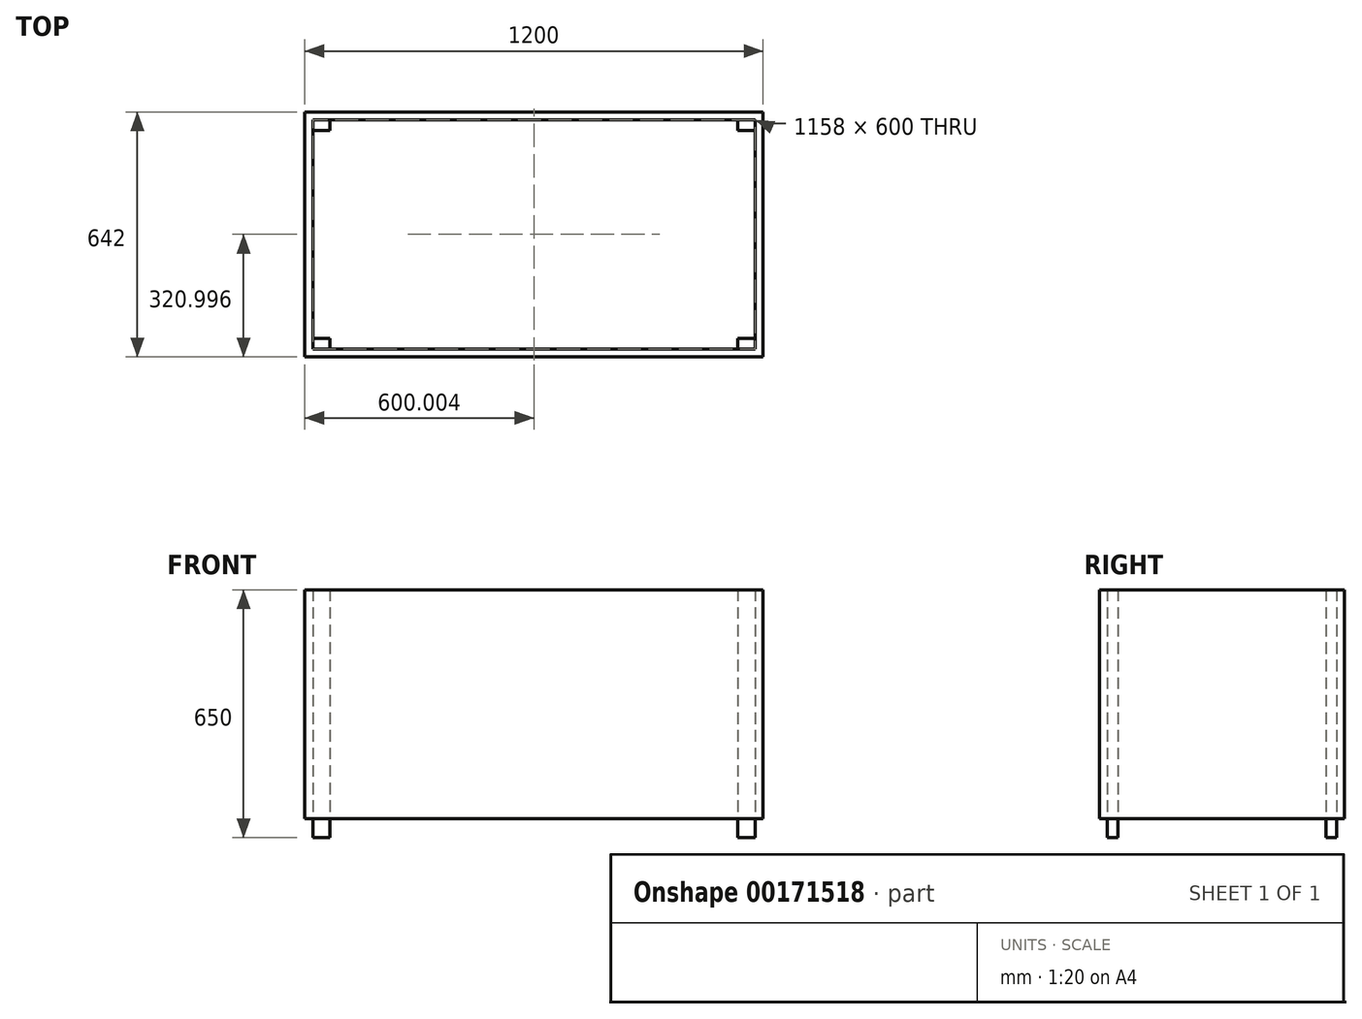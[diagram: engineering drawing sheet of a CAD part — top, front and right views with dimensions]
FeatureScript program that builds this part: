
annotation { "Feature Type Name" : "Feature", "Feature Type Description" : "" }
export const myFeature = defineFeature(function(context is Context, id is Id, definition is map)
    precondition{}
    {
        {
            var Q0;
            Q0=qCreatedBy(makeId("Top.planeOp"),FACE);
            var sketch = newSketch(context, id + "F0", { "sketchPlane" : qUnion([Q0])});
            skLineSegment(sketch, "E0.bottom", {"start": v(-516.42, -156.54) * mm, "end": v(683.58, -156.54) * mm});
            skLineSegment(sketch, "E0.top", {"start": v(-516.42, -177.54) * mm, "end": v(683.58, -177.54) * mm});
            skLineSegment(sketch, "E0.left", {"start": v(-516.42, -156.54) * mm, "end": v(-516.42, -177.54) * mm});
            skLineSegment(sketch, "E0.right", {"start": v(683.58, -156.54) * mm, "end": v(683.58, -177.54) * mm});
            skLineSegment(sketch, "E1.bottom", {"start": v(683.58, 464.46) * mm, "end": v(-516.42, 464.46) * mm});
            skLineSegment(sketch, "E1.top", {"start": v(683.58, 443.46) * mm, "end": v(-516.42, 443.46) * mm});
            skLineSegment(sketch, "E1.left", {"start": v(683.58, 464.46) * mm, "end": v(683.58, 443.46) * mm});
            skLineSegment(sketch, "E1.right", {"start": v(-516.42, 464.46) * mm, "end": v(-516.42, 443.46) * mm});
            skLineSegment(sketch, "E2.bottom", {"start": v(-516.42, 443.46) * mm, "end": v(-495.42, 443.46) * mm});
            skLineSegment(sketch, "E2.top", {"start": v(-516.42, -156.54) * mm, "end": v(-495.42, -156.54) * mm});
            skLineSegment(sketch, "E2.left", {"start": v(-516.42, 443.46) * mm, "end": v(-516.42, -156.54) * mm});
            skLineSegment(sketch, "E2.right", {"start": v(-495.42, 443.46) * mm, "end": v(-495.42, -156.54) * mm});
            skLineSegment(sketch, "E3.bottom", {"start": v(662.58, 443.46) * mm, "end": v(683.58, 443.46) * mm});
            skLineSegment(sketch, "E3.top", {"start": v(662.58, -156.54) * mm, "end": v(683.58, -156.54) * mm});
            skLineSegment(sketch, "E3.left", {"start": v(662.58, 443.46) * mm, "end": v(662.58, -156.54) * mm});
            skLineSegment(sketch, "E3.right", {"start": v(683.58, 443.46) * mm, "end": v(683.58, -156.54) * mm});
            skSolve(sketch);
        }
        {
            var Q0;
            Q0 = qSketchRegion(id + "F0", true);
            extrude(context, id + "F1", {"entities" : qUnion([Q0]), "depth" : 600 * mm});
        }
        {
            var Q0;
            Q0=qCreatedBy(makeId("Top.planeOp"),FACE);
            var sketch = newSketch(context, id + "F2", { "sketchPlane" : qUnion([Q0])});
            skLineSegment(sketch, "E4.bottom", {"start": v(-495.42, 443.46) * mm, "end": v(-450.42, 443.46) * mm});
            skLineSegment(sketch, "E4.top", {"start": v(-495.42, 415.46) * mm, "end": v(-450.42, 415.46) * mm});
            skLineSegment(sketch, "E4.left", {"start": v(-495.42, 443.46) * mm, "end": v(-495.42, 415.46) * mm});
            skLineSegment(sketch, "E4.right", {"start": v(-450.42, 443.46) * mm, "end": v(-450.42, 415.46) * mm});
            skLineSegment(sketch, "E5.bottom", {"start": v(617.58, 443.46) * mm, "end": v(662.58, 443.46) * mm});
            skLineSegment(sketch, "E5.top", {"start": v(617.58, 415.46) * mm, "end": v(662.58, 415.46) * mm});
            skLineSegment(sketch, "E5.left", {"start": v(617.58, 443.46) * mm, "end": v(617.58, 415.46) * mm});
            skLineSegment(sketch, "E5.right", {"start": v(662.58, 443.46) * mm, "end": v(662.58, 415.46) * mm});
            skLineSegment(sketch, "E6.bottom", {"start": v(617.58, -128.54) * mm, "end": v(662.58, -128.54) * mm});
            skLineSegment(sketch, "E6.top", {"start": v(617.58, -156.54) * mm, "end": v(662.58, -156.54) * mm});
            skLineSegment(sketch, "E6.left", {"start": v(617.58, -128.54) * mm, "end": v(617.58, -156.54) * mm});
            skLineSegment(sketch, "E6.right", {"start": v(662.58, -128.54) * mm, "end": v(662.58, -156.54) * mm});
            skLineSegment(sketch, "E7.bottom", {"start": v(-495.42, -128.54) * mm, "end": v(-450.42, -128.54) * mm});
            skLineSegment(sketch, "E7.top", {"start": v(-495.42, -156.54) * mm, "end": v(-450.42, -156.54) * mm});
            skLineSegment(sketch, "E7.left", {"start": v(-495.42, -128.54) * mm, "end": v(-495.42, -156.54) * mm});
            skLineSegment(sketch, "E7.right", {"start": v(-450.42, -128.54) * mm, "end": v(-450.42, -156.54) * mm});
            skSolve(sketch);
        }
        {
            var Q0;
            Q0 = qSketchRegion(id + "F2", true);
            extrude(context, id + "F3", {"entities" : qUnion([Q0]), "depth" : 600 * mm});
        }
        {
            var Q0;
            Q0 = qSketchRegion(id + "F2", true);
            extrude(context, id + "F4", {"entities" : qUnion([Q0]), "oppositeDirection" : true, "depth" : 50 * mm});
        }
    });
